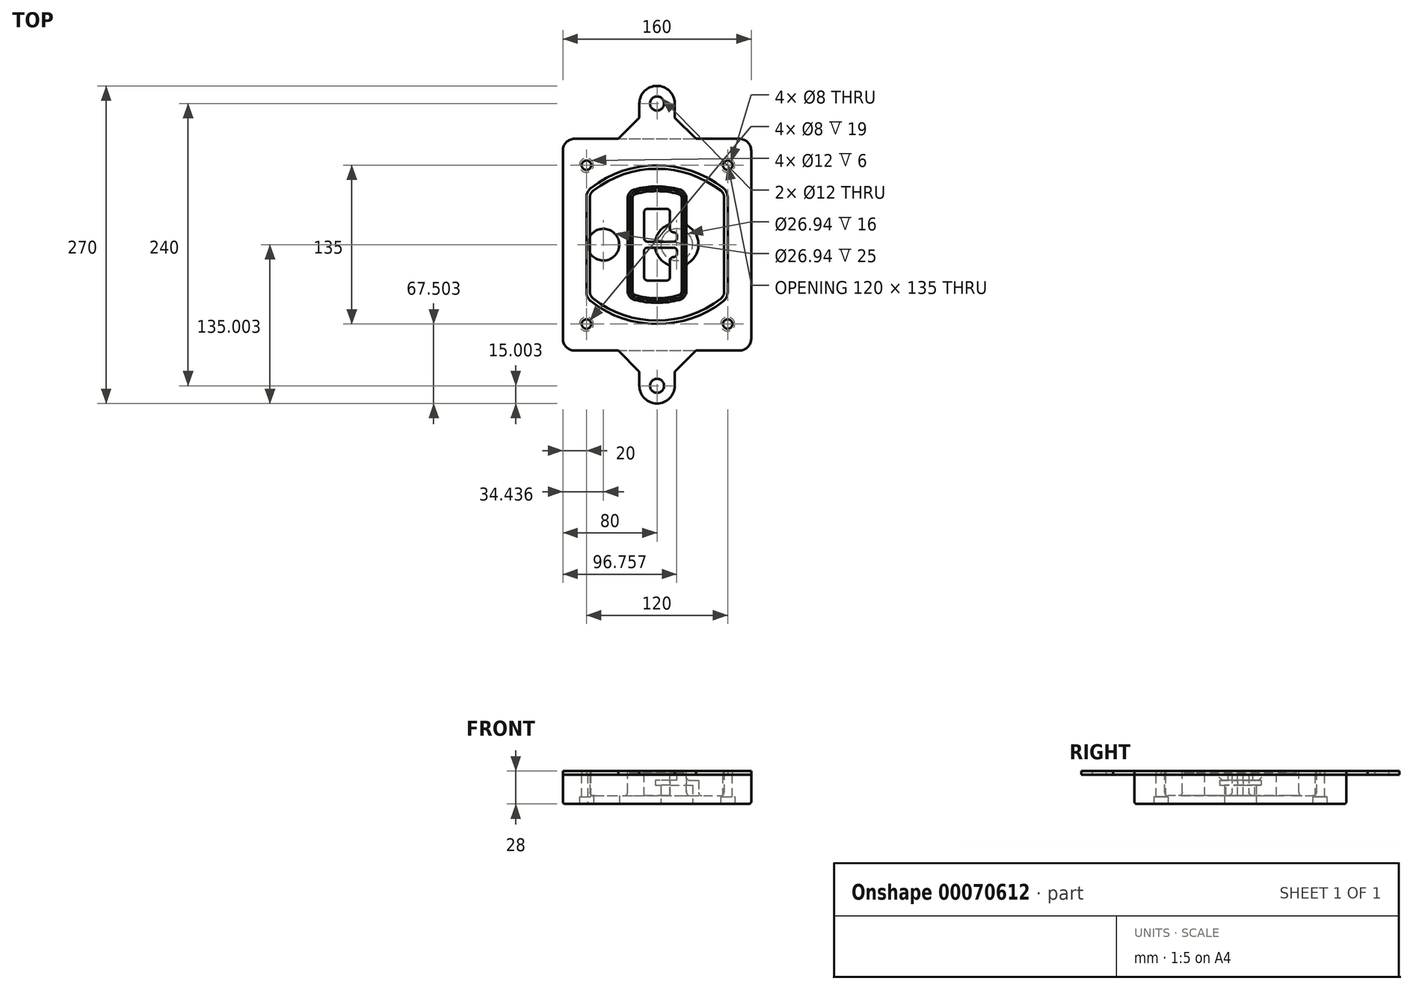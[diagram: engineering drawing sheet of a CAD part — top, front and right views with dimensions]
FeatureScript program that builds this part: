
annotation { "Feature Type Name" : "Feature", "Feature Type Description" : "" }
export const myFeature = defineFeature(function(context is Context, id is Id, definition is map)
    precondition{}
    {
        {
            var Q0;
            Q0=qCreatedBy(makeId("Top.planeOp"),FACE);
            var sketch = newSketch(context, id + "F0", { "sketchPlane" : qUnion([Q0])});
            skPoint(sketch, "E0.rect.middle", {"position": v(0, 0) * mm});
            skLineSegment(sketch, "E1.bottom", {"start": v(24.05, 28.38) * mm, "end": v(164.05, 28.38) * mm});
            skLineSegment(sketch, "E1.top", {"start": v(24.05, 208.38) * mm, "end": v(164.05, 208.38) * mm});
            skLineSegment(sketch, "E1.left", {"start": v(14.05, 38.38) * mm, "end": v(14.05, 198.38) * mm});
            skLineSegment(sketch, "E1.right", {"start": v(174.05, 38.38) * mm, "end": v(174.05, 198.38) * mm});
            skLineSegment(sketch, "E2", {"start": v(14.05, 208.38) * mm, "end": v(174.05, 28.38) * mm, "construction": true});
            skLineSegment(sketch, "E3", {"start": v(174.05, 208.38) * mm, "end": v(14.05, 28.38) * mm, "construction": true});
            skCircle(sketch, "E4", {"center": v(34.05, 185.88) * mm, "radius": 4 * mm});
            skCircle(sketch, "E5", {"center": v(154.05, 185.88) * mm, "radius": 4 * mm});
            skCircle(sketch, "E6", {"center": v(154.05, 50.88) * mm, "radius": 4 * mm});
            skCircle(sketch, "E7", {"center": v(34.05, 50.88) * mm, "radius": 4 * mm});
            skLineSegment(sketch, "E8", {"start": v(34.05, 185.88) * mm, "end": v(154.05, 185.88) * mm, "construction": true});
            skLineSegment(sketch, "E9", {"start": v(154.05, 185.88) * mm, "end": v(154.05, 50.88) * mm, "construction": true});
            skLineSegment(sketch, "E10", {"start": v(154.05, 50.88) * mm, "end": v(34.05, 50.88) * mm, "construction": true});
            skLineSegment(sketch, "E11", {"start": v(34.05, 50.88) * mm, "end": v(34.05, 185.88) * mm, "construction": true});
            skLineSegment(sketch, "E12", {"start": v(34.05, 158.68) * mm, "end": v(34.05, 78.09) * mm});
            skLineSegment(sketch, "E13", {"start": v(154.05, 158.68) * mm, "end": v(154.05, 78.09) * mm});
            skArc(sketch, "E14", {"start": v(150.2, 166.56) * mm, "mid": v(94.05, 185.88) * mm, "end": v(37.9, 166.56) * mm});
            skArc(sketch, "E15", {"start": v(37.9, 70.2) * mm, "mid": v(94.05, 50.88) * mm, "end": v(150.2, 70.2) * mm});
            skLineSegment(sketch, "E16", {"start": v(34.05, 118.38) * mm, "end": v(154.05, 118.38) * mm, "construction": true});
            skPoint(sketch, "E17.visualSharp", {"position": v(34.05, 73.38) * mm});
            skArc(sketch, "E17.filletArc", {"start": v(34.05, 78.09) * mm, "mid": v(35.06, 73.7) * mm, "end": v(37.9, 70.2) * mm});
            skPoint(sketch, "E18.visualSharp", {"position": v(34.05, 163.38) * mm});
            skArc(sketch, "E18.filletArc", {"start": v(37.9, 166.56) * mm, "mid": v(35.06, 163.06) * mm, "end": v(34.05, 158.68) * mm});
            skPoint(sketch, "E19.visualSharp", {"position": v(154.05, 163.38) * mm});
            skArc(sketch, "E19.filletArc", {"start": v(154.05, 158.68) * mm, "mid": v(153.04, 163.06) * mm, "end": v(150.2, 166.56) * mm});
            skPoint(sketch, "E20.visualSharp", {"position": v(154.05, 73.38) * mm});
            skArc(sketch, "E20.filletArc", {"start": v(150.2, 70.2) * mm, "mid": v(153.04, 73.7) * mm, "end": v(154.05, 78.09) * mm});
            skPoint(sketch, "E21.visualSharp", {"position": v(14.05, 208.38) * mm});
            skArc(sketch, "E21.filletArc", {"start": v(24.05, 208.38) * mm, "mid": v(16.98, 205.45) * mm, "end": v(14.05, 198.38) * mm});
            skPoint(sketch, "E22.visualSharp", {"position": v(174.05, 208.38) * mm});
            skArc(sketch, "E22.filletArc", {"start": v(174.05, 198.38) * mm, "mid": v(171.12, 205.45) * mm, "end": v(164.05, 208.38) * mm});
            skPoint(sketch, "E23.visualSharp", {"position": v(174.05, 28.38) * mm});
            skArc(sketch, "E23.filletArc", {"start": v(164.05, 28.38) * mm, "mid": v(171.12, 31.31) * mm, "end": v(174.05, 38.38) * mm});
            skPoint(sketch, "E24.visualSharp", {"position": v(14.05, 28.38) * mm});
            skArc(sketch, "E24.filletArc", {"start": v(14.05, 38.38) * mm, "mid": v(16.98, 31.31) * mm, "end": v(24.05, 28.38) * mm});
            skArc(sketch, "E25.0", {"start": v(151.05, 158.68) * mm, "mid": v(150.34, 161.75) * mm, "end": v(148.36, 164.2) * mm});
            skLineSegment(sketch, "E25.1", {"start": v(151.05, 158.68) * mm, "end": v(151.05, 78.09) * mm});
            skArc(sketch, "E25.2", {"start": v(148.36, 72.57) * mm, "mid": v(150.34, 75.02) * mm, "end": v(151.05, 78.09) * mm});
            skArc(sketch, "E25.3", {"start": v(39.74, 72.57) * mm, "mid": v(94.05, 53.88) * mm, "end": v(148.36, 72.57) * mm});
            skArc(sketch, "E25.4", {"start": v(37.05, 78.09) * mm, "mid": v(37.76, 75.02) * mm, "end": v(39.74, 72.57) * mm});
            skArc(sketch, "E25.5", {"start": v(148.36, 164.2) * mm, "mid": v(94.05, 182.88) * mm, "end": v(39.74, 164.2) * mm});
            skLineSegment(sketch, "E25.6", {"start": v(37.05, 158.68) * mm, "end": v(37.05, 78.09) * mm});
            skArc(sketch, "E25.7", {"start": v(39.74, 164.2) * mm, "mid": v(37.76, 161.75) * mm, "end": v(37.05, 158.68) * mm});
            skArc(sketch, "E26.0", {"start": v(35.43, 169.71) * mm, "mid": v(31.47, 164.82) * mm, "end": v(30.05, 158.68) * mm});
            skArc(sketch, "E26.1", {"start": v(152.67, 169.71) * mm, "mid": v(94.05, 189.88) * mm, "end": v(35.43, 169.71) * mm});
            skArc(sketch, "E26.2", {"start": v(158.05, 158.68) * mm, "mid": v(156.63, 164.82) * mm, "end": v(152.67, 169.71) * mm});
            skLineSegment(sketch, "E26.3", {"start": v(158.05, 158.68) * mm, "end": v(158.05, 78.09) * mm});
            skArc(sketch, "E26.4", {"start": v(152.67, 67.05) * mm, "mid": v(156.63, 71.95) * mm, "end": v(158.05, 78.09) * mm});
            skLineSegment(sketch, "E26.5", {"start": v(30.05, 158.68) * mm, "end": v(30.05, 78.09) * mm});
            skArc(sketch, "E26.6", {"start": v(35.43, 67.05) * mm, "mid": v(94.05, 46.88) * mm, "end": v(152.67, 67.05) * mm});
            skArc(sketch, "E26.7", {"start": v(30.05, 78.09) * mm, "mid": v(31.47, 71.95) * mm, "end": v(35.43, 67.05) * mm});
            skSolve(sketch);
        }
        {
            var Q0;
            Q0=makeQuery(id+"F0.imprint","IMPRINT",FACE,{"disambiguationData":[TD([[makeQuery(id+"F0.imprint","IMPRINT",EDGE,{"derivedFrom":sQuery(id+"F0.wireOp",EDGE,"E1.bottom")}),1.0]])]});
            var Q1;
            Q1=makeQuery(id+"F0.imprint","IMPRINT",FACE,{"disambiguationData":[TD([[makeQuery(id+"F0.imprint","IMPRINT",EDGE,{"derivedFrom":sQuery(id+"F0.wireOp",EDGE,"E12")}),1.0]])]});
            var Q2;
            Q2=makeQuery(id+"F0.imprint","IMPRINT",FACE,{"disambiguationData":[TD([[makeQuery(id+"F0.imprint","IMPRINT",EDGE,{"derivedFrom":sQuery(id+"F0.wireOp",EDGE,"E25.0")}),1.0]])]});
            var Q3;
            Q3=makeQuery(id+"F0.imprint","IMPRINT",FACE,{"disambiguationData":[TD([[makeQuery(id+"F0.imprint","IMPRINT",EDGE,{"derivedFrom":sQuery(id+"F0.wireOp",EDGE,"E12")}),-1.0]])]});
            extrude(context, id + "F1", {"entities" : qUnion([Q0, Q1, Q2, Q3]), "oppositeDirection" : true, "depth" : 25 * mm});
        }
        {
            var Q0;
            Q0=makeQuery(id+"F0.imprint","IMPRINT",FACE,{"disambiguationData":[TD([[makeQuery(id+"F0.imprint","IMPRINT",EDGE,{"derivedFrom":sQuery(id+"F0.wireOp",EDGE,"E12")}),1.0]])]});
            extrude(context, id + "F2", {"entities" : qUnion([Q0]), "operationType" : NewBodyOperationType.ADD, "depth" : 3 * mm});
        }
        {
            var Q0;
            Q0=makeQuery(id+"F0.imprint","IMPRINT",FACE,{"disambiguationData":[TD([[makeQuery(id+"F0.imprint","IMPRINT",EDGE,{"derivedFrom":sQuery(id+"F0.wireOp",EDGE,"E25.0")}),1.0]])]});
            extrude(context, id + "F3", {"entities" : qUnion([Q0]), "operationType" : NewBodyOperationType.REMOVE, "oppositeDirection" : true, "depth" : 18 * mm});
        }
        {
            var Q0;
            Q0=makeQuery(id+"F2.opExtrude","CAP_FACE",FACE,{"disambiguationData":[OSD([sQuery(id+"F0.wireOp",EDGE,"E12"),sQuery(id+"F0.wireOp",EDGE,"E13"),sQuery(id+"F0.wireOp",EDGE,"E14"),sQuery(id+"F0.wireOp",EDGE,"E15"),sQuery(id+"F0.wireOp",EDGE,"E17.filletArc"),sQuery(id+"F0.wireOp",EDGE,"E18.filletArc"),sQuery(id+"F0.wireOp",EDGE,"E19.filletArc"),sQuery(id+"F0.wireOp",EDGE,"E20.filletArc"),sQuery(id+"F0.wireOp",EDGE,"E25.0"),sQuery(id+"F0.wireOp",EDGE,"E25.1"),sQuery(id+"F0.wireOp",EDGE,"E25.2"),sQuery(id+"F0.wireOp",EDGE,"E25.3"),sQuery(id+"F0.wireOp",EDGE,"E25.4"),sQuery(id+"F0.wireOp",EDGE,"E25.5"),sQuery(id+"F0.wireOp",EDGE,"E25.6"),sQuery(id+"F0.wireOp",EDGE,"E25.7")])],"isStart":false});
            var sketch = newSketch(context, id + "F4", { "sketchPlane" : qUnion([Q0])});
            skArc(sketch, "E27.0", {"start": v(74.97, 71.41) * mm, "mid": v(94.05, 68.88) * mm, "end": v(113.13, 71.41) * mm});
            skArc(sketch, "E28.0", {"start": v(113.13, 165.35) * mm, "mid": v(94.05, 167.88) * mm, "end": v(74.97, 165.35) * mm});
            skLineSegment(sketch, "E29", {"start": v(69.05, 157.63) * mm, "end": v(69.05, 79.14) * mm});
            skLineSegment(sketch, "E30", {"start": v(119.05, 157.63) * mm, "end": v(119.05, 79.14) * mm});
            skLineSegment(sketch, "E31", {"start": v(69.05, 163.48) * mm, "end": v(119.05, 163.48) * mm, "construction": true});
            skLineSegment(sketch, "E32", {"start": v(69.05, 73.28) * mm, "end": v(119.05, 73.28) * mm, "construction": true});
            skPoint(sketch, "E33.visualSharp", {"position": v(69.05, 163.48) * mm});
            skArc(sketch, "E33.filletArc", {"start": v(74.97, 165.35) * mm, "mid": v(70.7, 162.5) * mm, "end": v(69.05, 157.63) * mm});
            skPoint(sketch, "E34.visualSharp", {"position": v(119.05, 163.48) * mm});
            skArc(sketch, "E34.filletArc", {"start": v(119.05, 157.63) * mm, "mid": v(117.4, 162.5) * mm, "end": v(113.13, 165.35) * mm});
            skPoint(sketch, "E35.visualSharp", {"position": v(119.05, 73.28) * mm});
            skArc(sketch, "E35.filletArc", {"start": v(113.13, 71.41) * mm, "mid": v(117.4, 74.27) * mm, "end": v(119.05, 79.14) * mm});
            skPoint(sketch, "E36.visualSharp", {"position": v(69.05, 73.28) * mm});
            skArc(sketch, "E36.filletArc", {"start": v(69.05, 79.14) * mm, "mid": v(70.7, 74.27) * mm, "end": v(74.97, 71.41) * mm});
            skArc(sketch, "E37.0", {"start": v(148.36, 164.2) * mm, "mid": v(94.05, 182.88) * mm, "end": v(39.74, 164.2) * mm});
            skArc(sketch, "E37.1", {"start": v(39.74, 164.2) * mm, "mid": v(37.76, 161.75) * mm, "end": v(37.05, 158.68) * mm});
            skLineSegment(sketch, "E37.2", {"start": v(37.05, 158.68) * mm, "end": v(37.05, 78.09) * mm});
            skArc(sketch, "E37.3", {"start": v(37.05, 78.09) * mm, "mid": v(37.76, 75.02) * mm, "end": v(39.74, 72.57) * mm});
            skArc(sketch, "E37.4", {"start": v(39.74, 72.57) * mm, "mid": v(94.05, 53.88) * mm, "end": v(148.36, 72.57) * mm});
            skArc(sketch, "E37.5", {"start": v(148.36, 72.57) * mm, "mid": v(150.34, 75.02) * mm, "end": v(151.05, 78.09) * mm});
            skLineSegment(sketch, "E37.6", {"start": v(151.05, 158.68) * mm, "end": v(151.05, 78.09) * mm});
            skArc(sketch, "E37.7", {"start": v(151.05, 158.68) * mm, "mid": v(150.34, 161.75) * mm, "end": v(148.36, 164.2) * mm});
            skLineSegment(sketch, "E38.0", {"start": v(117.05, 157.63) * mm, "end": v(117.05, 79.14) * mm});
            skArc(sketch, "E38.1", {"start": v(112.61, 73.34) * mm, "mid": v(115.81, 75.49) * mm, "end": v(117.05, 79.14) * mm});
            skArc(sketch, "E38.2", {"start": v(75.49, 73.34) * mm, "mid": v(94.05, 70.88) * mm, "end": v(112.61, 73.34) * mm});
            skArc(sketch, "E38.3", {"start": v(71.05, 79.14) * mm, "mid": v(72.29, 75.49) * mm, "end": v(75.49, 73.34) * mm});
            skLineSegment(sketch, "E38.4", {"start": v(71.05, 157.63) * mm, "end": v(71.05, 79.14) * mm});
            skArc(sketch, "E38.5", {"start": v(117.05, 157.63) * mm, "mid": v(115.81, 161.28) * mm, "end": v(112.61, 163.42) * mm});
            skArc(sketch, "E38.6", {"start": v(75.49, 163.42) * mm, "mid": v(72.29, 161.28) * mm, "end": v(71.05, 157.63) * mm});
            skArc(sketch, "E38.7", {"start": v(112.61, 163.42) * mm, "mid": v(94.05, 165.88) * mm, "end": v(75.49, 163.42) * mm});
            skArc(sketch, "E39.0", {"start": v(115.05, 157.63) * mm, "mid": v(114.23, 160.06) * mm, "end": v(112.1, 161.5) * mm});
            skLineSegment(sketch, "E39.1", {"start": v(115.05, 157.63) * mm, "end": v(115.05, 79.14) * mm});
            skArc(sketch, "E39.2", {"start": v(112.1, 75.27) * mm, "mid": v(114.23, 76.7) * mm, "end": v(115.05, 79.14) * mm});
            skArc(sketch, "E39.3", {"start": v(76, 75.27) * mm, "mid": v(94.05, 72.88) * mm, "end": v(112.1, 75.27) * mm});
            skArc(sketch, "E39.4", {"start": v(73.05, 79.14) * mm, "mid": v(73.87, 76.7) * mm, "end": v(76, 75.27) * mm});
            skArc(sketch, "E39.5", {"start": v(112.1, 161.5) * mm, "mid": v(94.05, 163.88) * mm, "end": v(76, 161.5) * mm});
            skLineSegment(sketch, "E39.6", {"start": v(73.05, 157.63) * mm, "end": v(73.05, 79.14) * mm});
            skArc(sketch, "E39.7", {"start": v(76, 161.5) * mm, "mid": v(73.87, 160.06) * mm, "end": v(73.05, 157.63) * mm});
            skLineSegment(sketch, "E40", {"start": v(69.05, 118.38) * mm, "end": v(119.05, 118.38) * mm, "construction": true});
            skLineSegment(sketch, "E41", {"start": v(83.05, 123.88) * mm, "end": v(83.05, 145.88) * mm});
            skLineSegment(sketch, "E42", {"start": v(86.05, 148.88) * mm, "end": v(102.05, 148.88) * mm});
            skLineSegment(sketch, "E43", {"start": v(105.05, 145.88) * mm, "end": v(105.05, 131.88) * mm});
            skLineSegment(sketch, "E44", {"start": v(108.05, 128.88) * mm, "end": v(108.05, 128.88) * mm});
            skLineSegment(sketch, "E45", {"start": v(111.05, 125.88) * mm, "end": v(111.05, 123.88) * mm});
            skLineSegment(sketch, "E46", {"start": v(108.05, 120.88) * mm, "end": v(86.05, 120.88) * mm});
            skPoint(sketch, "E47.visualSharp", {"position": v(83.05, 148.88) * mm});
            skArc(sketch, "E47.filletArc", {"start": v(86.05, 148.88) * mm, "mid": v(83.93, 148) * mm, "end": v(83.05, 145.88) * mm});
            skPoint(sketch, "E48.visualSharp", {"position": v(105.05, 148.88) * mm});
            skArc(sketch, "E48.filletArc", {"start": v(105.05, 145.88) * mm, "mid": v(104.17, 148) * mm, "end": v(102.05, 148.88) * mm});
            skPoint(sketch, "E49.visualSharp", {"position": v(105.05, 128.88) * mm});
            skArc(sketch, "E49.filletArc", {"start": v(105.05, 131.88) * mm, "mid": v(105.93, 129.76) * mm, "end": v(108.05, 128.88) * mm});
            skPoint(sketch, "E50.visualSharp", {"position": v(111.05, 128.88) * mm});
            skArc(sketch, "E50.filletArc", {"start": v(111.05, 125.88) * mm, "mid": v(110.17, 128) * mm, "end": v(108.05, 128.88) * mm});
            skPoint(sketch, "E51.visualSharp", {"position": v(111.05, 120.88) * mm});
            skArc(sketch, "E51.filletArc", {"start": v(108.05, 120.88) * mm, "mid": v(110.17, 121.76) * mm, "end": v(111.05, 123.88) * mm});
            skPoint(sketch, "E52.visualSharp", {"position": v(83.05, 120.88) * mm});
            skArc(sketch, "E52.filletArc", {"start": v(83.05, 123.88) * mm, "mid": v(83.93, 121.76) * mm, "end": v(86.05, 120.88) * mm});
            skLineSegment(sketch, "E53.0.MirrorCS", {"start": v(108.05, 115.88) * mm, "end": v(86.05, 115.88) * mm});
            skArc(sketch, "E54.0.MirrorCS", {"start": v(83.05, 112.88) * mm, "mid": v(83.93, 115) * mm, "end": v(86.05, 115.88) * mm});
            skLineSegment(sketch, "E55.0.MirrorCS", {"start": v(83.05, 112.88) * mm, "end": v(83.05, 90.88) * mm});
            skArc(sketch, "E56.0.MirrorCS", {"start": v(86.05, 87.88) * mm, "mid": v(83.93, 88.76) * mm, "end": v(83.05, 90.88) * mm});
            skLineSegment(sketch, "E57.0.MirrorCS", {"start": v(86.05, 87.88) * mm, "end": v(102.05, 87.88) * mm});
            skArc(sketch, "E58.0.MirrorCS", {"start": v(105.05, 90.88) * mm, "mid": v(104.17, 88.76) * mm, "end": v(102.05, 87.88) * mm});
            skLineSegment(sketch, "E59.0.MirrorCS", {"start": v(105.05, 90.88) * mm, "end": v(105.05, 104.88) * mm});
            skArc(sketch, "E60.0.MirrorCS", {"start": v(105.05, 104.88) * mm, "mid": v(105.93, 107) * mm, "end": v(108.05, 107.88) * mm});
            skArc(sketch, "E61.0.MirrorCS", {"start": v(111.05, 110.88) * mm, "mid": v(110.17, 108.76) * mm, "end": v(108.05, 107.88) * mm});
            skLineSegment(sketch, "E62.0.MirrorCS", {"start": v(111.05, 110.88) * mm, "end": v(111.05, 112.88) * mm});
            skArc(sketch, "E63.0.MirrorCS", {"start": v(108.05, 115.88) * mm, "mid": v(110.17, 115) * mm, "end": v(111.05, 112.88) * mm});
            skSolve(sketch);
        }
        {
            var Q0;
            Q0=makeQuery(id+"F4.imprint","IMPRINT",FACE,{"disambiguationData":[TD([[makeQuery(id+"F4.imprint","IMPRINT",EDGE,{"derivedFrom":sQuery(id+"F4.wireOp",EDGE,"E27.0")}),1.0]])]});
            var Q1;
            Q1=makeQuery(id+"F4.imprint","IMPRINT",FACE,{"disambiguationData":[TD([[makeQuery(id+"F4.imprint","IMPRINT",EDGE,{"derivedFrom":sQuery(id+"F4.wireOp",EDGE,"E38.0")}),-1.0]])]});
            var Q2;
            Q2=makeQuery(id+"F4.imprint","IMPRINT",FACE,{"disambiguationData":[TD([[makeQuery(id+"F4.imprint","IMPRINT",EDGE,{"derivedFrom":sQuery(id+"F4.wireOp",EDGE,"E39.0")}),1.0]])]});
            extrude(context, id + "F5", {"entities" : qUnion([Q0, Q1, Q2]), "operationType" : NewBodyOperationType.ADD, "endBound" : BoundingType.UP_TO_NEXT, "oppositeDirection" : true, "depth" : 25 * mm});
        }
        {
            var Q0;
            Q0=makeQuery(id+"F4.imprint","IMPRINT",FACE,{"disambiguationData":[TD([[makeQuery(id+"F4.imprint","IMPRINT",EDGE,{"derivedFrom":sQuery(id+"F4.wireOp",EDGE,"E38.0")}),-1.0]])]});
            extrude(context, id + "F6", {"entities" : qUnion([Q0]), "operationType" : NewBodyOperationType.REMOVE, "oppositeDirection" : true, "depth" : 2 * mm});
        }
        {
            var Q0;
            Q0=makeQuery(id+"F1.opExtrude","CAP_FACE",FACE,{"disambiguationData":[OSD([sQuery(id+"F0.wireOp",EDGE,"E1.bottom"),sQuery(id+"F0.wireOp",EDGE,"E1.top"),sQuery(id+"F0.wireOp",EDGE,"E1.left"),sQuery(id+"F0.wireOp",EDGE,"E1.right"),sQuery(id+"F0.wireOp",EDGE,"E4"),sQuery(id+"F0.wireOp",EDGE,"E5"),sQuery(id+"F0.wireOp",EDGE,"E6"),sQuery(id+"F0.wireOp",EDGE,"E7"),sQuery(id+"F0.wireOp",EDGE,"E21.filletArc"),sQuery(id+"F0.wireOp",EDGE,"E22.filletArc"),sQuery(id+"F0.wireOp",EDGE,"E23.filletArc"),sQuery(id+"F0.wireOp",EDGE,"E24.filletArc")])],"isStart":false});
            var sketch = newSketch(context, id + "F7", { "sketchPlane" : qUnion([Q0])});
            skCircle(sketch, "E64", {"center": v(110.8, -118.38) * mm, "radius": 13.47 * mm});
            skCircle(sketch, "E65", {"center": v(48.49, -118.38) * mm, "radius": 13.47 * mm});
            skLineSegment(sketch, "E66", {"start": v(174.05, -118.38) * mm, "end": v(14.05, -118.38) * mm});
            skCircle(sketch, "E67", {"center": v(110.8, -118.38) * mm, "radius": 18.47 * mm});
            skCircle(sketch, "E68", {"center": v(154.05, -185.88) * mm, "radius": 6 * mm});
            skCircle(sketch, "E69", {"center": v(34.05, -185.88) * mm, "radius": 6 * mm});
            skCircle(sketch, "E70", {"center": v(34.05, -50.88) * mm, "radius": 6 * mm});
            skCircle(sketch, "E71", {"center": v(154.05, -50.88) * mm, "radius": 6 * mm});
            skSolve(sketch);
        }
        {
            var Q0;
            {var subQ1=sQuery(id+"F7.wireOp",EDGE,"E66");var subQ4=sQuery(id+"F7.wireOp",EDGE,"E64");var subQ6=makeQuery(id+"F7.imprint","INTERSECT",VERTEX,{"disambiguationData":[OD(0.0)],"derivedFrom":[subQ4,subQ1]});Q0=makeQuery(id+"F7.imprint","IMPRINT",FACE,{"disambiguationData":[TD([[makeQuery(id+"F7.imprint","IMPRINT",EDGE,{"disambiguationData":[TD([[subQ6,-1.0]])],"derivedFrom":subQ4}),-1.0]])]});}
            var Q1;
            {var subQ0=sQuery(id+"F7.wireOp",EDGE,"E66");var subQ1=sQuery(id+"F7.wireOp",EDGE,"E64");var subQ3=makeQuery(id+"F7.imprint","INTERSECT",VERTEX,{"disambiguationData":[OD(0.0)],"derivedFrom":[subQ1,subQ0]});Q1=makeQuery(id+"F7.imprint","IMPRINT",FACE,{"disambiguationData":[TD([[makeQuery(id+"F7.imprint","IMPRINT",EDGE,{"disambiguationData":[TD([[subQ3,-1.0]])],"derivedFrom":subQ1}),1.0]])]});}
            var Q2;
            {var subQ0=sQuery(id+"F7.wireOp",EDGE,"E66");var subQ1=sQuery(id+"F7.wireOp",EDGE,"E64");var subQ3=makeQuery(id+"F7.imprint","INTERSECT",VERTEX,{"disambiguationData":[OD(0.0)],"derivedFrom":[subQ1,subQ0]});Q2=makeQuery(id+"F7.imprint","IMPRINT",FACE,{"disambiguationData":[TD([[makeQuery(id+"F7.imprint","IMPRINT",EDGE,{"disambiguationData":[TD([[subQ3,1.0]])],"derivedFrom":subQ1}),1.0]])]});}
            var Q3;
            {var subQ1=sQuery(id+"F7.wireOp",EDGE,"E66");var subQ4=sQuery(id+"F7.wireOp",EDGE,"E64");var subQ6=makeQuery(id+"F7.imprint","INTERSECT",VERTEX,{"disambiguationData":[OD(0.0)],"derivedFrom":[subQ4,subQ1]});Q3=makeQuery(id+"F7.imprint","IMPRINT",FACE,{"disambiguationData":[TD([[makeQuery(id+"F7.imprint","IMPRINT",EDGE,{"disambiguationData":[TD([[subQ6,1.0]])],"derivedFrom":subQ4}),-1.0]])]});}
            extrude(context, id + "F8", {"entities" : qUnion([Q0, Q1, Q2, Q3]), "operationType" : NewBodyOperationType.ADD, "oppositeDirection" : true, "depth" : 20 * mm});
        }
        {
            var Q0;
            {var subQ0=sQuery(id+"F7.wireOp",EDGE,"E66");var subQ1=sQuery(id+"F7.wireOp",EDGE,"E64");var subQ3=makeQuery(id+"F7.imprint","INTERSECT",VERTEX,{"disambiguationData":[OD(0.0)],"derivedFrom":[subQ1,subQ0]});Q0=makeQuery(id+"F7.imprint","IMPRINT",FACE,{"disambiguationData":[TD([[makeQuery(id+"F7.imprint","IMPRINT",EDGE,{"disambiguationData":[TD([[subQ3,-1.0]])],"derivedFrom":subQ1}),1.0]])]});}
            var Q1;
            {var subQ0=sQuery(id+"F7.wireOp",EDGE,"E66");var subQ1=sQuery(id+"F7.wireOp",EDGE,"E64");var subQ3=makeQuery(id+"F7.imprint","INTERSECT",VERTEX,{"disambiguationData":[OD(0.0)],"derivedFrom":[subQ1,subQ0]});Q1=makeQuery(id+"F7.imprint","IMPRINT",FACE,{"disambiguationData":[TD([[makeQuery(id+"F7.imprint","IMPRINT",EDGE,{"disambiguationData":[TD([[subQ3,1.0]])],"derivedFrom":subQ1}),1.0]])]});}
            extrude(context, id + "F9", {"entities" : qUnion([Q0, Q1]), "operationType" : NewBodyOperationType.REMOVE, "oppositeDirection" : true, "depth" : 16 * mm});
        }
        {
            var Q0;
            {var subQ0=sQuery(id+"F7.wireOp",EDGE,"E66");var subQ1=sQuery(id+"F7.wireOp",EDGE,"E65");var subQ3=makeQuery(id+"F7.imprint","INTERSECT",VERTEX,{"disambiguationData":[OD(0.0)],"derivedFrom":[subQ1,subQ0]});Q0=makeQuery(id+"F7.imprint","IMPRINT",FACE,{"disambiguationData":[TD([[makeQuery(id+"F7.imprint","IMPRINT",EDGE,{"disambiguationData":[TD([[subQ3,-1.0]])],"derivedFrom":subQ1}),1.0]])]});}
            var Q1;
            {var subQ0=sQuery(id+"F7.wireOp",EDGE,"E66");var subQ1=sQuery(id+"F7.wireOp",EDGE,"E65");var subQ3=makeQuery(id+"F7.imprint","INTERSECT",VERTEX,{"disambiguationData":[OD(0.0)],"derivedFrom":[subQ1,subQ0]});Q1=makeQuery(id+"F7.imprint","IMPRINT",FACE,{"disambiguationData":[TD([[makeQuery(id+"F7.imprint","IMPRINT",EDGE,{"disambiguationData":[TD([[subQ3,1.0]])],"derivedFrom":subQ1}),1.0]])]});}
            extrude(context, id + "F10", {"entities" : qUnion([Q0, Q1]), "operationType" : NewBodyOperationType.REMOVE, "oppositeDirection" : true, "depth" : 25 * mm});
        }
        {
            var Q0;
            Q0=makeQuery(id+"F7.imprint","IMPRINT",FACE,{"disambiguationData":[TD([[makeQuery(id+"F7.imprint","IMPRINT",EDGE,{"derivedFrom":sQuery(id+"F7.wireOp",EDGE,"E68")}),1.0]])]});
            var Q1;
            Q1=makeQuery(id+"F7.imprint","IMPRINT",FACE,{"disambiguationData":[TD([[makeQuery(id+"F7.imprint","IMPRINT",EDGE,{"derivedFrom":makeQuery(id+"F1.opExtrude","CAP_EDGE",EDGE,{"disambiguationData":[OSD([sQuery(id+"F0.wireOp",EDGE,"E5")])],"isStart":false})}),-1.0]])]});
            var Q2;
            Q2=makeQuery(id+"F7.imprint","IMPRINT",FACE,{"disambiguationData":[TD([[makeQuery(id+"F7.imprint","IMPRINT",EDGE,{"derivedFrom":sQuery(id+"F7.wireOp",EDGE,"E69")}),1.0]])]});
            var Q3;
            Q3=makeQuery(id+"F7.imprint","IMPRINT",FACE,{"disambiguationData":[TD([[makeQuery(id+"F7.imprint","IMPRINT",EDGE,{"derivedFrom":makeQuery(id+"F1.opExtrude","CAP_EDGE",EDGE,{"disambiguationData":[OSD([sQuery(id+"F0.wireOp",EDGE,"E4")])],"isStart":false})}),-1.0]])]});
            var Q4;
            Q4=makeQuery(id+"F7.imprint","IMPRINT",FACE,{"disambiguationData":[TD([[makeQuery(id+"F7.imprint","IMPRINT",EDGE,{"derivedFrom":sQuery(id+"F7.wireOp",EDGE,"E70")}),1.0]])]});
            var Q5;
            Q5=makeQuery(id+"F7.imprint","IMPRINT",FACE,{"disambiguationData":[TD([[makeQuery(id+"F7.imprint","IMPRINT",EDGE,{"derivedFrom":makeQuery(id+"F1.opExtrude","CAP_EDGE",EDGE,{"disambiguationData":[OSD([sQuery(id+"F0.wireOp",EDGE,"E7")])],"isStart":false})}),-1.0]])]});
            var Q6;
            Q6=makeQuery(id+"F7.imprint","IMPRINT",FACE,{"disambiguationData":[TD([[makeQuery(id+"F7.imprint","IMPRINT",EDGE,{"derivedFrom":sQuery(id+"F7.wireOp",EDGE,"E71")}),1.0]])]});
            var Q7;
            Q7=makeQuery(id+"F7.imprint","IMPRINT",FACE,{"disambiguationData":[TD([[makeQuery(id+"F7.imprint","IMPRINT",EDGE,{"derivedFrom":makeQuery(id+"F1.opExtrude","CAP_EDGE",EDGE,{"disambiguationData":[OSD([sQuery(id+"F0.wireOp",EDGE,"E6")])],"isStart":false})}),-1.0]])]});
            extrude(context, id + "F11", {"entities" : qUnion([Q0, Q1, Q2, Q3, Q4, Q5, Q6, Q7]), "operationType" : NewBodyOperationType.REMOVE, "oppositeDirection" : true, "depth" : 6 * mm});
        }
        {
            var Q0;
            Q0=makeQuery(id+"F9.boolean.opBoolean","COPY",FACE,{"derivedFrom":makeQuery(id+"F9.opExtrude","CAP_FACE",FACE,{"disambiguationData":[OSD([sQuery(id+"F7.wireOp",EDGE,"E64")])],"isStart":false})});
            var sketch = newSketch(context, id + "F12", { "sketchPlane" : qUnion([Q0])});
            skArc(sketch, "E72.0", {"start": v(105.05, -100.83) * mm, "mid": v(96.62, -106.56) * mm, "end": v(92.5, -115.88) * mm});
            skArc(sketch, "E72.1", {"start": v(92.5, -120.88) * mm, "mid": v(96.62, -130.2) * mm, "end": v(105.05, -135.93) * mm});
            skLineSegment(sketch, "E73", {"start": v(92.5, -120.88) * mm, "end": v(108.05, -120.88) * mm});
            skLineSegment(sketch, "E74.0", {"start": v(108.05, -115.88) * mm, "end": v(92.5, -115.88) * mm});
            skArc(sketch, "E74.1", {"start": v(108.05, -115.88) * mm, "mid": v(110.17, -115) * mm, "end": v(111.05, -112.88) * mm});
            skLineSegment(sketch, "E74.2", {"start": v(111.05, -110.88) * mm, "end": v(111.05, -112.88) * mm});
            skArc(sketch, "E74.3", {"start": v(111.05, -110.88) * mm, "mid": v(110.17, -108.76) * mm, "end": v(108.05, -107.88) * mm});
            skArc(sketch, "E74.4", {"start": v(105.05, -104.88) * mm, "mid": v(105.93, -107) * mm, "end": v(108.05, -107.88) * mm});
            skLineSegment(sketch, "E74.5", {"start": v(105.05, -100.83) * mm, "end": v(105.05, -104.88) * mm});
            skLineSegment(sketch, "E74.7", {"start": v(108.05, -120.88) * mm, "end": v(92.5, -120.88) * mm});
            skArc(sketch, "E74.8", {"start": v(108.05, -120.88) * mm, "mid": v(110.17, -121.76) * mm, "end": v(111.05, -123.88) * mm});
            skLineSegment(sketch, "E74.9", {"start": v(111.05, -125.88) * mm, "end": v(111.05, -123.88) * mm});
            skArc(sketch, "E74.10", {"start": v(111.05, -125.88) * mm, "mid": v(110.17, -128) * mm, "end": v(108.05, -128.88) * mm});
            skArc(sketch, "E74.11", {"start": v(105.05, -131.88) * mm, "mid": v(105.93, -129.76) * mm, "end": v(108.05, -128.88) * mm});
            skLineSegment(sketch, "E74.12", {"start": v(105.05, -135.93) * mm, "end": v(105.05, -131.88) * mm});
            skPoint(sketch, "E75.orphan", {"position": v(105.05, -145.88) * mm});
            skPoint(sketch, "E76.orphan", {"position": v(86.05, -120.88) * mm});
            skPoint(sketch, "E77.orphan", {"position": v(86.05, -115.88) * mm});
            skPoint(sketch, "E78.orphan", {"position": v(105.05, -90.88) * mm});
            skSolve(sketch);
        }
        {
            var Q0;
            {var subQ7=sQuery(id+"F12.wireOp",EDGE,"E72.0");var subQ14=sQuery(id+"F12.wireOp",EDGE,"E72.1");var subQ16=sQuery(id+"F12.wireOp",EDGE,"E74.1");var subQ18=sQuery(id+"F12.wireOp",EDGE,"E74.8");Q0=qUnion([makeQuery(id+"F12.imprint","IMPRINT",FACE,{"disambiguationData":[TD([[makeQuery(id+"F12.imprint","IMPRINT",EDGE,{"derivedFrom":subQ7}),1.0]])]}),makeQuery(id+"F12.imprint","IMPRINT",FACE,{"disambiguationData":[TD([[makeQuery(id+"F12.imprint","IMPRINT",EDGE,{"derivedFrom":subQ14}),1.0]])]}),makeQuery(id+"F12.imprint","IMPRINT",FACE,{"disambiguationData":[TD([[makeQuery(id+"F12.imprint","IMPRINT",EDGE,{"derivedFrom":subQ16}),1.0]])]}),makeQuery(id+"F12.imprint","IMPRINT",FACE,{"disambiguationData":[TD([[makeQuery(id+"F12.imprint","IMPRINT",EDGE,{"derivedFrom":subQ18}),-1.0]])]})]);}
            var Q1;
            Q1=makeQuery(id+"F5.boolean.opBoolean","SPLIT",FACE,{"disambiguationData":[TD([makeQuery(id+"F5.opExtrude","SWEPT_FACE",FACE,{"disambiguationData":[OSD([sQuery(id+"F4.wireOp",EDGE,"E41")])]})])],"derivedFrom":makeQuery(id+"F3.boolean.opBoolean","COPY",FACE,{"derivedFrom":makeQuery(id+"F3.opExtrude","CAP_FACE",FACE,{"disambiguationData":[OSD([sQuery(id+"F0.wireOp",EDGE,"E25.0"),sQuery(id+"F0.wireOp",EDGE,"E25.1"),sQuery(id+"F0.wireOp",EDGE,"E25.2"),sQuery(id+"F0.wireOp",EDGE,"E25.3"),sQuery(id+"F0.wireOp",EDGE,"E25.4"),sQuery(id+"F0.wireOp",EDGE,"E25.5"),sQuery(id+"F0.wireOp",EDGE,"E25.6"),sQuery(id+"F0.wireOp",EDGE,"E25.7")])],"isStart":false})})});
            extrude(context, id + "F13", {"entities" : qUnion([Q0]), "operationType" : NewBodyOperationType.REMOVE, "endBound" : BoundingType.UP_TO_SURFACE, "endBoundEntityFace" : qUnion([Q1]), "depth" : 25 * mm});
        }
        {
            var Q0;
            Q0=makeQuery(id+"F3.boolean.opBoolean","COPY",EDGE,{"derivedFrom":makeQuery(id+"F3.opExtrude","CAP_EDGE",EDGE,{"disambiguationData":[OSD([sQuery(id+"F0.wireOp",EDGE,"E25.6")])],"isStart":false})});
            var Q1;
            Q1=makeQuery(id+"F8.boolean.opBoolean","INTERSECT",EDGE,{"derivedFrom":[makeQuery(id+"F5.opExtrude","SWEPT_FACE",FACE,{"disambiguationData":[OSD([sQuery(id+"F4.wireOp",EDGE,"E30")])]}),makeQuery(id+"F8.opExtrude","CAP_FACE",FACE,{"disambiguationData":[OSD([sQuery(id+"F7.wireOp",EDGE,"E67")])],"isStart":false})]});
            var Q2;
            Q2=makeQuery(id+"F8.boolean.opBoolean","INTERSECT",EDGE,{"disambiguationData":[OD(1.0)],"derivedFrom":[makeQuery(id+"F5.opExtrude","SWEPT_FACE",FACE,{"disambiguationData":[OSD([sQuery(id+"F4.wireOp",EDGE,"E30")])]}),makeQuery(id+"F8.opExtrude","SWEPT_FACE",FACE,{"disambiguationData":[OSD([sQuery(id+"F7.wireOp",EDGE,"E67")])]})]});
            var Q3;
            {var subQ0=sQuery(id+"F4.wireOp",EDGE,"E30");Q3=makeQuery(id+"F8.boolean.opBoolean","SPLIT",EDGE,{"disambiguationData":[TD([makeQuery(id+"F5.opExtrude","SWEPT_FACE",FACE,{"disambiguationData":[OSD([sQuery(id+"F4.wireOp",EDGE,"E35.filletArc")])]})])],"derivedFrom":makeQuery(id+"F5.opExtrude","CAP_EDGE",EDGE,{"disambiguationData":[OSD([subQ0])],"isStart":false})});}
            var Q4;
            {var subQ0=sQuery(id+"F0.wireOp",EDGE,"E25.7");var subQ1=sQuery(id+"F0.wireOp",EDGE,"E25.1");var subQ2=sQuery(id+"F0.wireOp",EDGE,"E25.6");var subQ3=sQuery(id+"F0.wireOp",EDGE,"E25.5");var subQ4=sQuery(id+"F0.wireOp",EDGE,"E25.4");var subQ5=sQuery(id+"F0.wireOp",EDGE,"E25.0");var subQ6=sQuery(id+"F0.wireOp",EDGE,"E25.2");var subQ7=sQuery(id+"F0.wireOp",EDGE,"E25.3");Q4=makeQuery(id+"F8.boolean.opBoolean","INTERSECT",EDGE,{"derivedFrom":[makeQuery(id+"F5.boolean.opBoolean","SPLIT",FACE,{"disambiguationData":[TD([makeQuery(id+"F2.opExtrude","SWEPT_FACE",FACE,{"disambiguationData":[OSD([subQ5])]})])],"derivedFrom":makeQuery(id+"F3.boolean.opBoolean","COPY",FACE,{"derivedFrom":makeQuery(id+"F3.opExtrude","CAP_FACE",FACE,{"disambiguationData":[OSD([subQ5,subQ1,subQ6,subQ7,subQ4,subQ3,subQ2,subQ0])],"isStart":false})})}),makeQuery(id+"F8.opExtrude","SWEPT_FACE",FACE,{"disambiguationData":[OSD([sQuery(id+"F7.wireOp",EDGE,"E67")])]})]});}
            var Q5;
            Q5=makeQuery(id+"F8.boolean.opBoolean","INTERSECT",EDGE,{"disambiguationData":[OD(0.0)],"derivedFrom":[makeQuery(id+"F5.opExtrude","SWEPT_FACE",FACE,{"disambiguationData":[OSD([sQuery(id+"F4.wireOp",EDGE,"E30")])]}),makeQuery(id+"F8.opExtrude","SWEPT_FACE",FACE,{"disambiguationData":[OSD([sQuery(id+"F7.wireOp",EDGE,"E67")])]})]});
            fillet(context, id + "F14", {"entities" : qUnion([Q0, Q1, Q2, Q3, Q4, Q5]), "radius" : 3 * mm, "tangentPropagation" : true, "allowEdgeOverflow" : false});
        }
        {
            var Q0;
            Q0=makeQuery(id+"F1.opExtrude","CAP_EDGE",EDGE,{"disambiguationData":[OSD([sQuery(id+"F0.wireOp",EDGE,"E1.bottom")])],"isStart":false});
            fillet(context, id + "F15", {"entities" : qUnion([Q0]), "radius" : 2 * mm, "tangentPropagation" : true, "allowEdgeOverflow" : false});
        }
        {
            var Q0;
            {var subQ0=sQuery(id+"F0.wireOp",EDGE,"E22.filletArc");var subQ1=sQuery(id+"F0.wireOp",EDGE,"E7");var subQ2=sQuery(id+"F0.wireOp",EDGE,"E6");var subQ3=sQuery(id+"F0.wireOp",EDGE,"E5");var subQ4=sQuery(id+"F0.wireOp",EDGE,"E4");var subQ5=sQuery(id+"F0.wireOp",EDGE,"E1.bottom");var subQ6=sQuery(id+"F0.wireOp",EDGE,"E21.filletArc");var subQ7=sQuery(id+"F0.wireOp",EDGE,"E1.top");var subQ8=sQuery(id+"F0.wireOp",EDGE,"E1.left");var subQ9=sQuery(id+"F0.wireOp",EDGE,"E1.right");var subQ10=sQuery(id+"F0.wireOp",EDGE,"E23.filletArc");var subQ11=sQuery(id+"F0.wireOp",EDGE,"E24.filletArc");Q0=makeQuery(id+"F2.boolean.opBoolean","SPLIT",FACE,{"disambiguationData":[TD([makeQuery(id+"F1.opExtrude","SWEPT_FACE",FACE,{"disambiguationData":[OSD([subQ5])]})])],"derivedFrom":makeQuery(id+"F1.opExtrude","CAP_FACE",FACE,{"disambiguationData":[OSD([subQ5,subQ7,subQ8,subQ9,subQ4,subQ3,subQ2,subQ1,subQ6,subQ0,subQ10,subQ11])],"isStart":true})});}
            var sketch = newSketch(context, id + "F16", { "sketchPlane" : qUnion([Q0])});
            skSolve(sketch);
        }
        {
            var Q0;
            Q0=makeQuery(id+"F16.imprint","IMPRINT",FACE,{"disambiguationData":[TD([[makeQuery(id+"F16.imprint","IMPRINT",EDGE,{"derivedFrom":makeQuery(id+"F1.opExtrude","CAP_EDGE",EDGE,{"disambiguationData":[OSD([sQuery(id+"F0.wireOp",EDGE,"E1.bottom")])],"isStart":true})}),1.0]])]});
            var sketch = newSketch(context, id + "F17", { "sketchPlane" : qUnion([Q0])});
            skLineSegment(sketch, "E79.0", {"start": v(14.05, 38.38) * mm, "end": v(14.05, 198.38) * mm});
            skArc(sketch, "E79.1", {"start": v(24.05, 208.38) * mm, "mid": v(16.98, 205.45) * mm, "end": v(14.05, 198.38) * mm});
            skLineSegment(sketch, "E79.2", {"start": v(24.05, 208.38) * mm, "end": v(164.05, 208.38) * mm});
            skArc(sketch, "E79.3", {"start": v(174.05, 198.38) * mm, "mid": v(171.12, 205.45) * mm, "end": v(164.05, 208.38) * mm});
            skLineSegment(sketch, "E79.4", {"start": v(174.05, 38.38) * mm, "end": v(174.05, 198.38) * mm});
            skArc(sketch, "E79.5", {"start": v(164.05, 28.38) * mm, "mid": v(171.12, 31.31) * mm, "end": v(174.05, 38.38) * mm});
            skLineSegment(sketch, "E79.6", {"start": v(24.05, 28.38) * mm, "end": v(164.05, 28.38) * mm});
            skArc(sketch, "E79.7", {"start": v(14.05, 38.38) * mm, "mid": v(16.98, 31.31) * mm, "end": v(24.05, 28.38) * mm});
            skCircle(sketch, "E79.8", {"center": v(34.05, 50.88) * mm, "radius": 4 * mm});
            skCircle(sketch, "E79.9", {"center": v(34.05, 185.88) * mm, "radius": 4 * mm});
            skCircle(sketch, "E79.10", {"center": v(154.05, 185.88) * mm, "radius": 4 * mm});
            skCircle(sketch, "E79.11", {"center": v(154.05, 50.88) * mm, "radius": 4 * mm});
            skArc(sketch, "E79.12", {"start": v(37.9, 70.2) * mm, "mid": v(94.05, 50.88) * mm, "end": v(150.2, 70.2) * mm});
            skArc(sketch, "E79.13", {"start": v(34.05, 78.09) * mm, "mid": v(35.06, 73.7) * mm, "end": v(37.9, 70.2) * mm});
            skLineSegment(sketch, "E79.14", {"start": v(34.05, 158.68) * mm, "end": v(34.05, 78.09) * mm});
            skArc(sketch, "E79.15", {"start": v(37.9, 166.56) * mm, "mid": v(35.06, 163.06) * mm, "end": v(34.05, 158.68) * mm});
            skArc(sketch, "E79.16", {"start": v(150.2, 166.56) * mm, "mid": v(94.05, 185.88) * mm, "end": v(37.9, 166.56) * mm});
            skArc(sketch, "E79.17", {"start": v(154.05, 158.68) * mm, "mid": v(153.04, 163.06) * mm, "end": v(150.2, 166.56) * mm});
            skLineSegment(sketch, "E79.18", {"start": v(154.05, 158.68) * mm, "end": v(154.05, 78.09) * mm});
            skArc(sketch, "E79.19", {"start": v(150.2, 70.2) * mm, "mid": v(153.04, 73.7) * mm, "end": v(154.05, 78.09) * mm});
            skLineSegment(sketch, "E80", {"start": v(94.05, 208.38) * mm, "end": v(94.05, 238.38) * mm, "construction": true});
            skArc(sketch, "E81", {"start": v(109.05, 238.38) * mm, "mid": v(94.05, 253.38) * mm, "end": v(79.05, 238.38) * mm});
            skCircle(sketch, "E82", {"center": v(94.05, 238.38) * mm, "radius": 6 * mm});
            skLineSegment(sketch, "E83", {"start": v(79.05, 238.38) * mm, "end": v(79.05, 226.38) * mm});
            skLineSegment(sketch, "E84", {"start": v(79.05, 226.38) * mm, "end": v(61.05, 208.38) * mm});
            skLineSegment(sketch, "E85", {"start": v(109.05, 238.38) * mm, "end": v(109.05, 226.38) * mm});
            skLineSegment(sketch, "E86", {"start": v(109.05, 226.38) * mm, "end": v(127.05, 208.38) * mm});
            skLineSegment(sketch, "E87", {"start": v(14.05, 118.38) * mm, "end": v(174.05, 118.38) * mm, "construction": true});
            skArc(sketch, "E88.MirrorCS", {"start": v(79.05, 238.38) * mm, "mid": v(94.05, 253.38) * mm, "end": v(109.05, 238.38) * mm});
            skLineSegment(sketch, "E89.MirrorCS", {"start": v(164.05, 208.38) * mm, "end": v(24.05, 208.38) * mm});
            skLineSegment(sketch, "E90.MirrorCS", {"start": v(174.05, 118.38) * mm, "end": v(14.05, 118.38) * mm, "construction": true});
            skLineSegment(sketch, "E91.MirrorCS", {"start": v(79.05, -1.62) * mm, "end": v(79.05, 10.38) * mm});
            skLineSegment(sketch, "E92.MirrorCS", {"start": v(109.05, -1.62) * mm, "end": v(109.05, 10.38) * mm});
            skCircle(sketch, "E93.MirrorC", {"center": v(94.05, -1.62) * mm, "radius": 6 * mm});
            skLineSegment(sketch, "E94.MirrorCS", {"start": v(109.05, 10.38) * mm, "end": v(127.05, 28.38) * mm});
            skLineSegment(sketch, "E95.MirrorCS", {"start": v(79.05, 10.38) * mm, "end": v(61.05, 28.38) * mm});
            skArc(sketch, "E96.MirrorCS", {"start": v(79.05, -1.62) * mm, "mid": v(94.05, -16.62) * mm, "end": v(109.05, -1.62) * mm});
            skArc(sketch, "E97.MirrorCS", {"start": v(109.05, -1.62) * mm, "mid": v(94.05, -16.62) * mm, "end": v(79.05, -1.62) * mm});
            skLineSegment(sketch, "E98.MirrorCS", {"start": v(94.05, 28.38) * mm, "end": v(94.05, -1.62) * mm, "construction": true});
            skSolve(sketch);
        }
        {
            var Q0;
            Q0 = qSketchRegion(id + "F17", true);
            var Q1;
            {var subQ0=sQuery(id+"F4.wireOp",EDGE,"E36.filletArc");var subQ1=sQuery(id+"F4.wireOp",EDGE,"E35.filletArc");var subQ2=sQuery(id+"F4.wireOp",EDGE,"E34.filletArc");var subQ3=sQuery(id+"F4.wireOp",EDGE,"E33.filletArc");var subQ4=sQuery(id+"F4.wireOp",EDGE,"E27.0");var subQ5=sQuery(id+"F4.wireOp",EDGE,"E30");var subQ6=sQuery(id+"F4.wireOp",EDGE,"E28.0");var subQ7=sQuery(id+"F4.wireOp",EDGE,"E29");Q1=makeQuery(id+"F6.boolean.opBoolean","SPLIT",FACE,{"disambiguationData":[TD([makeQuery(id+"F5.opExtrude","SWEPT_FACE",FACE,{"disambiguationData":[OSD([subQ4])]})])],"derivedFrom":makeQuery(id+"F5.opExtrude","CAP_FACE",FACE,{"disambiguationData":[OSD([subQ4,subQ6,subQ7,subQ5,subQ3,subQ2,subQ1,subQ0,sQuery(id+"F4.wireOp",EDGE,"E41"),sQuery(id+"F4.wireOp",EDGE,"E42"),sQuery(id+"F4.wireOp",EDGE,"E43"),sQuery(id+"F4.wireOp",EDGE,"E45"),sQuery(id+"F4.wireOp",EDGE,"E46"),sQuery(id+"F4.wireOp",EDGE,"E47.filletArc"),sQuery(id+"F4.wireOp",EDGE,"E48.filletArc"),sQuery(id+"F4.wireOp",EDGE,"E49.filletArc"),sQuery(id+"F4.wireOp",EDGE,"E50.filletArc"),sQuery(id+"F4.wireOp",EDGE,"E51.filletArc"),sQuery(id+"F4.wireOp",EDGE,"E52.filletArc"),sQuery(id+"F4.wireOp",EDGE,"E53.0.MirrorCS"),sQuery(id+"F4.wireOp",EDGE,"E54.0.MirrorCS"),sQuery(id+"F4.wireOp",EDGE,"E55.0.MirrorCS"),sQuery(id+"F4.wireOp",EDGE,"E56.0.MirrorCS"),sQuery(id+"F4.wireOp",EDGE,"E57.0.MirrorCS"),sQuery(id+"F4.wireOp",EDGE,"E58.0.MirrorCS"),sQuery(id+"F4.wireOp",EDGE,"E59.0.MirrorCS"),sQuery(id+"F4.wireOp",EDGE,"E60.0.MirrorCS"),sQuery(id+"F4.wireOp",EDGE,"E61.0.MirrorCS"),sQuery(id+"F4.wireOp",EDGE,"E62.0.MirrorCS"),sQuery(id+"F4.wireOp",EDGE,"E63.0.MirrorCS")])],"isStart":true})});}
            extrude(context, id + "F18", {"entities" : qUnion([Q0]), "endBound" : BoundingType.UP_TO_SURFACE, "endBoundEntityFace" : qUnion([Q1]), "depth" : 25 * mm});
        }
    });
